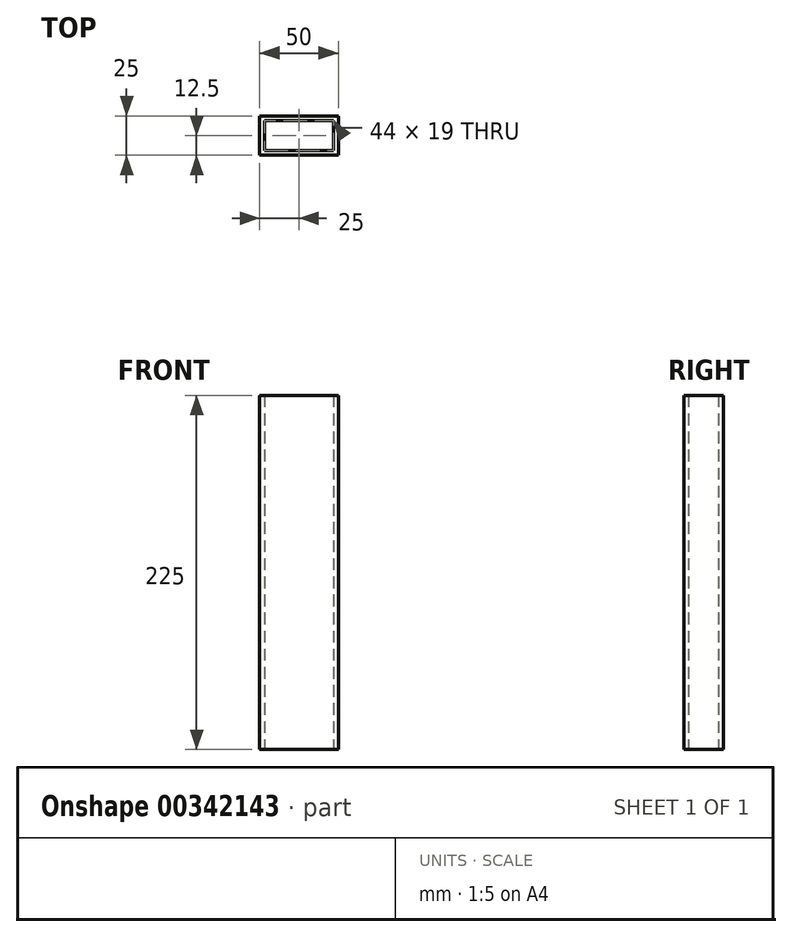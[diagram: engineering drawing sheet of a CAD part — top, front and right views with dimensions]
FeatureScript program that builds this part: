
annotation { "Feature Type Name" : "Feature", "Feature Type Description" : "" }
export const myFeature = defineFeature(function(context is Context, id is Id, definition is map)
    precondition{}
    {
        {
            var Q0;
            Q0=qCreatedBy(makeId("Top.planeOp"),FACE);
            var sketch = newSketch(context, id + "F0", { "sketchPlane" : qUnion([Q0])});
            skLineSegment(sketch, "E0.bottom", {"start": v(25, -12.5) * mm, "end": v(-25, -12.5) * mm});
            skLineSegment(sketch, "E0.top", {"start": v(25, 12.5) * mm, "end": v(-25, 12.5) * mm});
            skLineSegment(sketch, "E0.left", {"start": v(25, -12.5) * mm, "end": v(25, 12.5) * mm});
            skLineSegment(sketch, "E0.right", {"start": v(-25, -12.5) * mm, "end": v(-25, 12.5) * mm});
            skPoint(sketch, "E0.middle", {"position": v(0, 0) * mm});
            skLineSegment(sketch, "E1.bottom", {"start": v(22, -9.5) * mm, "end": v(-22, -9.5) * mm});
            skLineSegment(sketch, "E1.top", {"start": v(22, 9.5) * mm, "end": v(-22, 9.5) * mm});
            skLineSegment(sketch, "E1.left", {"start": v(22, -9.5) * mm, "end": v(22, 9.5) * mm});
            skLineSegment(sketch, "E1.right", {"start": v(-22, -9.5) * mm, "end": v(-22, 9.5) * mm});
            skSolve(sketch);
        }
        {
            var Q0;
            Q0=qSketchRegion(id+"F0",true);
            extrude(context, id + "F1", {"entities" : qUnion([Q0]), "endBound" : BoundingType.SYMMETRIC, "depth" : 225 * mm});
        }
    });
